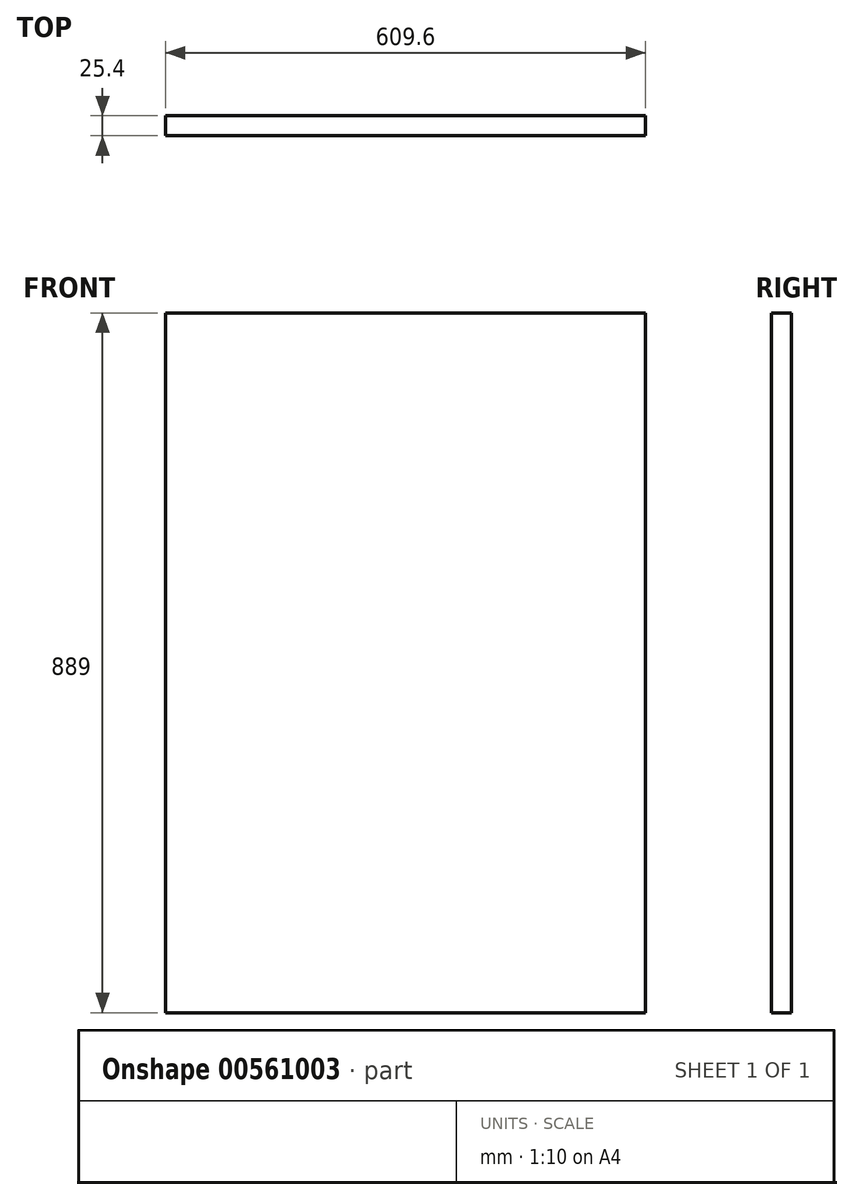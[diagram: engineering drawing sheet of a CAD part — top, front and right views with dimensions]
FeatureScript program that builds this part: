
annotation { "Feature Type Name" : "Feature", "Feature Type Description" : "" }
export const myFeature = defineFeature(function(context is Context, id is Id, definition is map)
    precondition{}
    {
        {
            var Q0;
            Q0=qCreatedBy(makeId("Front.planeOp"),FACE);
            var sketch = newSketch(context, id + "F0", { "sketchPlane" : qUnion([Q0])});
            skLineSegment(sketch, "E0.bottom", {"start": v(-304.8, 444.5) * mm, "end": v(304.8, 444.5) * mm});
            skLineSegment(sketch, "E0.top", {"start": v(-304.8, -444.5) * mm, "end": v(304.8, -444.5) * mm});
            skLineSegment(sketch, "E0.left", {"start": v(-304.8, 444.5) * mm, "end": v(-304.8, -444.5) * mm});
            skLineSegment(sketch, "E0.right", {"start": v(304.8, 444.5) * mm, "end": v(304.8, -444.5) * mm});
            skLineSegment(sketch, "E1", {"start": v(304.8, 444.5) * mm, "end": v(-304.8, -444.5) * mm, "construction": true});
            skSolve(sketch);
        }
        {
            var Q0;
            Q0 = qSketchRegion(id + "F0", true);
            extrude(context, id + "F1", {"entities" : qUnion([Q0]), "depth" : 25.4 * mm, "offsetDistance" : 25.4 * mm});
        }
    });
